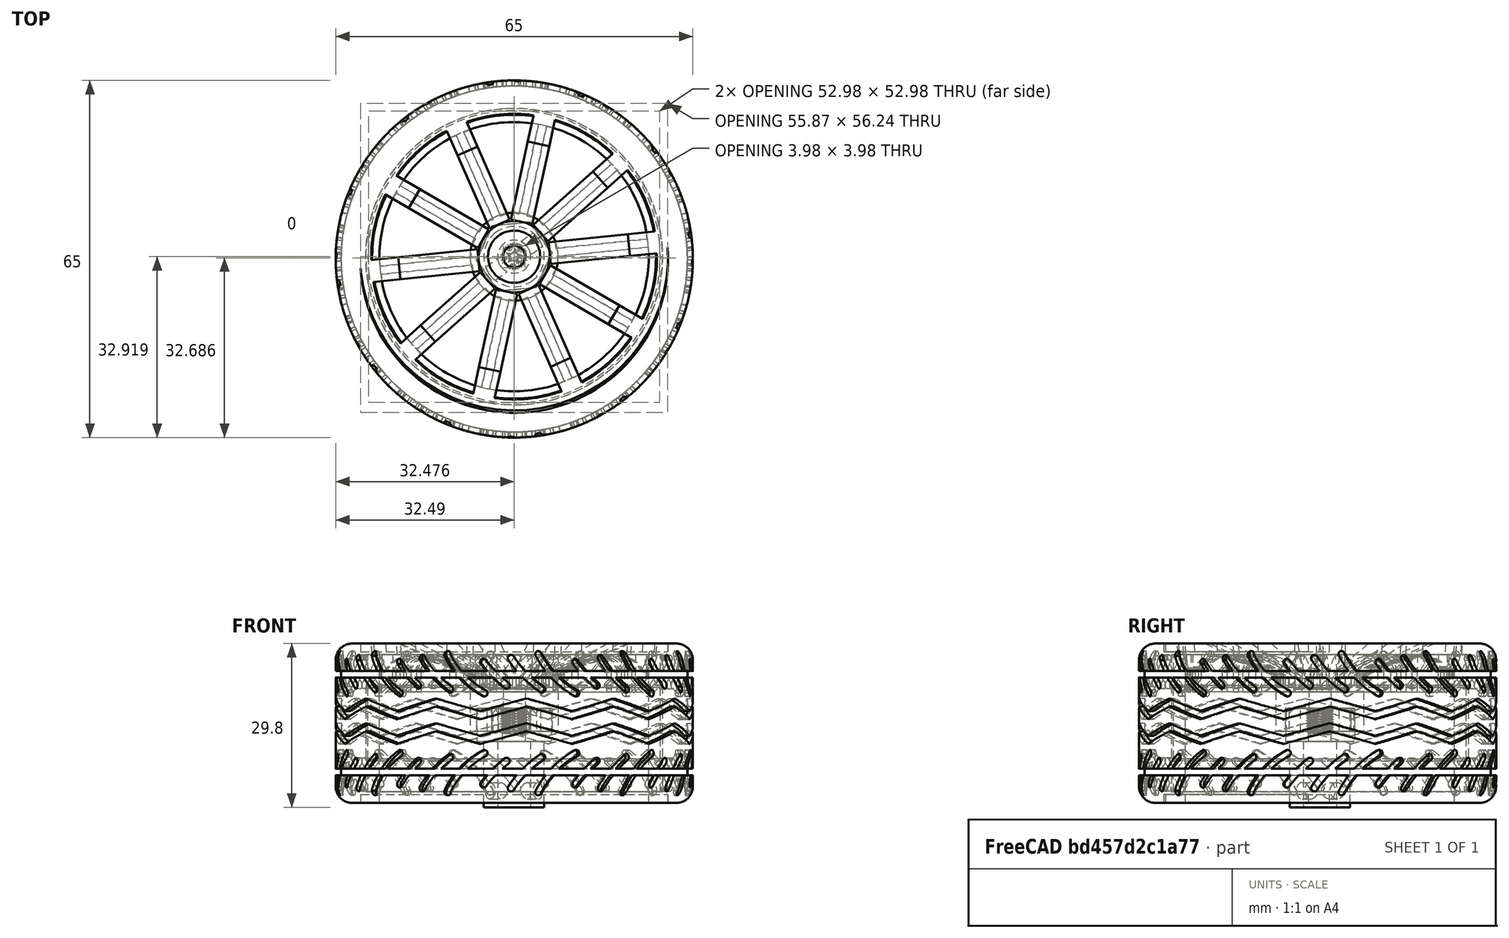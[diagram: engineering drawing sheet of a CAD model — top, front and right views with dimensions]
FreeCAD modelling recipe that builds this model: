
FCSTD DOCUMENT  (FreeCAD 0.17R13541 (Git))
Label: blue_wheel_with_adapter
License: All rights reserved
LicenseURL: http://en.wikipedia.org/wiki/All_rights_reserved
objects: Part::Feature×3, App::Part×1, Part::MultiFuse×1
note: 4 computed .brp shape members not serialized (recipe doc carries the construction recipe); baked Part::Feature solids carry a one-line shape summary decoded from their .brp

FEATURE [Part::Feature] Part__Feature  label="65mm tire"
  Placement = pos=(18.1044,52.2783,38.5614) rot=(0,0,1;1.63927rad)
  shape: bbox 70.19 x 70.19 x 29 mm, 870 faces (baked)
FEATURE [Part::Feature] Part__Feature001  label="blue_wheel_frame"
  Placement = pos=(18.0756,52.6985,38.5614) rot=(0.706655,0.035753,-0.706655;3.07012rad)
  shape: bbox 56 x 56 x 29 mm, 204 faces (baked)
FEATURE [Part::Feature] Part__Feature002  label="motor_adapter"
  Placement = pos=(18.0661,52.7117,35.2614) rot=(0,0,-1;0.947995rad)
  shape: bbox 13.69 x 12.61 x 18.32 mm, 62 faces (baked)
FEATURE [App::Part] blue_wheel_with_adapter
  Group = -> [Part__Feature,Part__Feature001,Part__Feature002]
  License = CC BY 3.0
  LicenseURL = http://creativecommons.org/licenses/by/3.0/
  Origin = -> Origin
FEATURE [Part::MultiFuse] Fusion
  Shapes = -> [Part__Feature,Part__Feature001,Part__Feature002]
